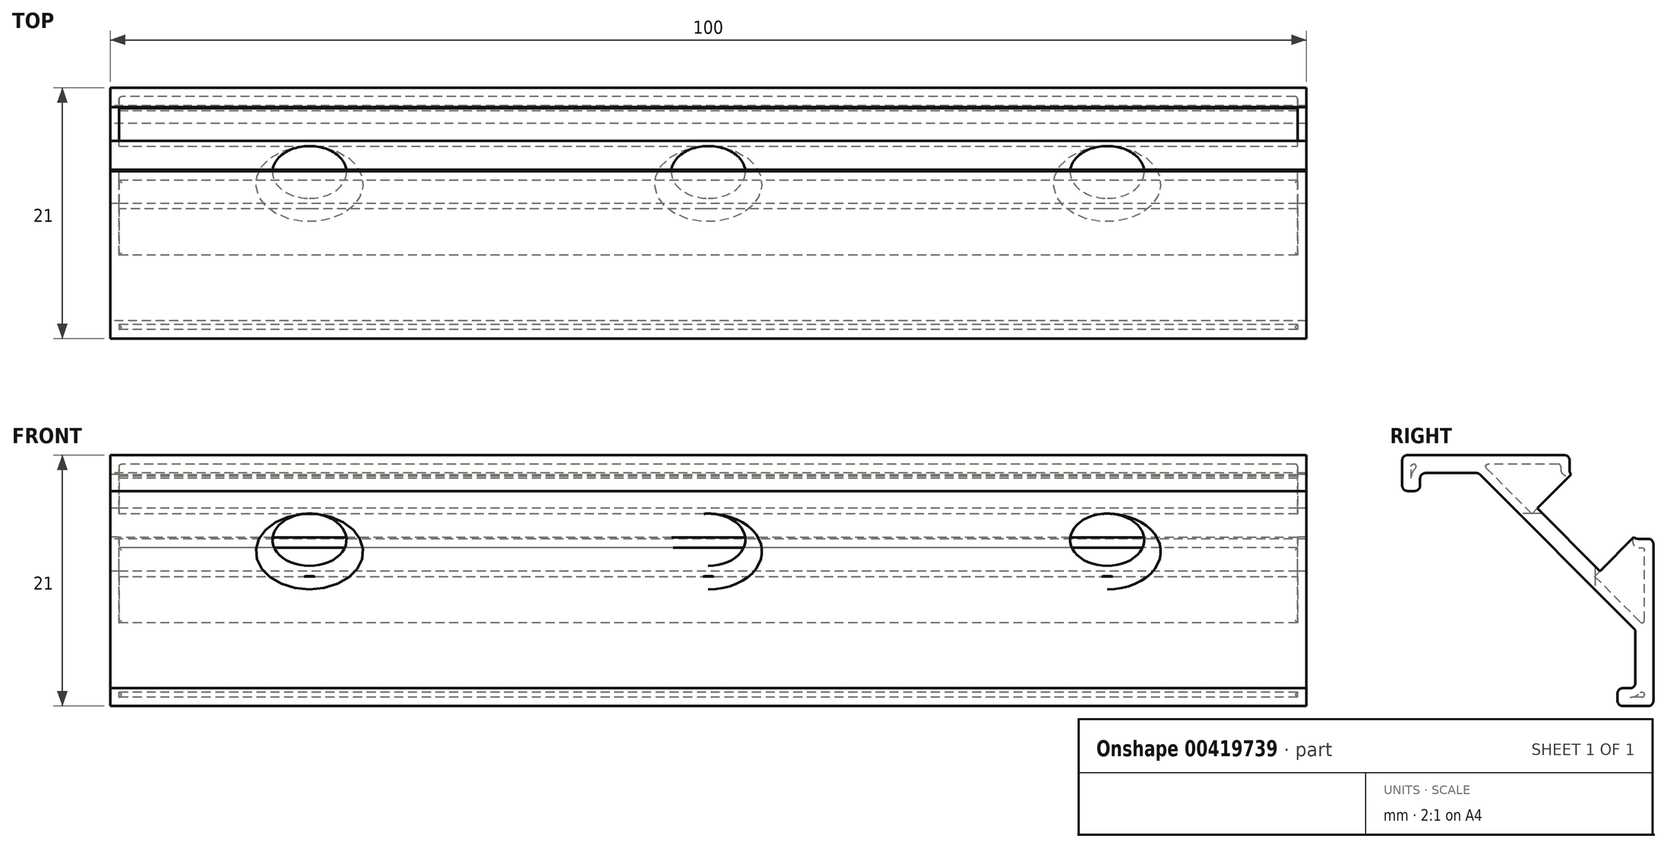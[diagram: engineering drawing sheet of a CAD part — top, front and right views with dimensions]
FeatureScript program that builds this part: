
annotation { "Feature Type Name" : "Feature", "Feature Type Description" : "" }
export const myFeature = defineFeature(function(context is Context, id is Id, definition is map)
    precondition{}
    {
        {
            var Q0;
            Q0=qCreatedBy(makeId("Right.planeOp"),FACE);
            var sketch = newSketch(context, id + "F0", { "sketchPlane" : qUnion([Q0])});
            skLineSegment(sketch, "E0.bottom", {"start": v(10.06, -10.5) * mm, "end": v(7.94, -10.5) * mm});
            skLineSegment(sketch, "E0.top", {"start": v(3.06, 10.5) * mm, "end": v(-10.06, 10.5) * mm});
            skLineSegment(sketch, "E0.left", {"start": v(10.5, -10.06) * mm, "end": v(10.5, 3.06) * mm});
            skPoint(sketch, "E0.middle", {"position": v(0, 0) * mm});
            skPoint(sketch, "E1.orphan", {"position": v(10.5, 10.5) * mm});
            skLineSegment(sketch, "E2.0", {"start": v(-4.3, 9) * mm, "end": v(-8.56, 9) * mm});
            skLineSegment(sketch, "E3.0", {"start": v(-4, 8.87) * mm, "end": v(8.87, -4) * mm});
            skLineSegment(sketch, "E4.0", {"start": v(9, -8.56) * mm, "end": v(9, -4.3) * mm});
            skLineSegment(sketch, "E5.0", {"start": v(8.56, -9) * mm, "end": v(7.94, -9) * mm});
            skLineSegment(sketch, "E6", {"start": v(3.5, 10.06) * mm, "end": v(3.5, 9.18) * mm});
            skLineSegment(sketch, "E7", {"start": v(9.18, 3.5) * mm, "end": v(10.06, 3.5) * mm});
            skLineSegment(sketch, "E8", {"start": v(-10.06, 7.5) * mm, "end": v(-9.44, 7.5) * mm});
            skLineSegment(sketch, "E9", {"start": v(7.5, -10.06) * mm, "end": v(7.5, -9.44) * mm});
            skLineSegment(sketch, "E10.trimOffspring", {"start": v(-9, 7.94) * mm, "end": v(-9, 8.56) * mm});
            skLineSegment(sketch, "E11.trimOffspring", {"start": v(-10.5, 7.94) * mm, "end": v(-10.5, 10.06) * mm});
            skPoint(sketch, "E12.trimOffspring.end.orphan", {"position": v(-10.5, -10.5) * mm});
            skLineSegment(sketch, "E13", {"start": v(3.63, 8.87) * mm, "end": v(8.87, 3.63) * mm});
            skPoint(sketch, "E14.visualSharp", {"position": v(3.5, 10.5) * mm});
            skArc(sketch, "E14.filletArc", {"start": v(3.5, 10.06) * mm, "mid": v(3.37, 10.37) * mm, "end": v(3.06, 10.5) * mm});
            skPoint(sketch, "E15.visualSharp", {"position": v(10.5, 3.5) * mm});
            skArc(sketch, "E15.filletArc", {"start": v(10.5, 3.06) * mm, "mid": v(10.37, 3.37) * mm, "end": v(10.06, 3.5) * mm});
            skPoint(sketch, "E16.visualSharp", {"position": v(3.5, 9) * mm});
            skArc(sketch, "E16.filletArc", {"start": v(3.5, 9.18) * mm, "mid": v(3.53, 9.01) * mm, "end": v(3.63, 8.87) * mm});
            skPoint(sketch, "E17.visualSharp", {"position": v(9, 3.5) * mm});
            skArc(sketch, "E17.filletArc", {"start": v(8.87, 3.63) * mm, "mid": v(9.01, 3.53) * mm, "end": v(9.18, 3.5) * mm});
            skPoint(sketch, "E18.orphan", {"position": v(-3.5, 10.5) * mm});
            skPoint(sketch, "E19.orphan", {"position": v(10.5, -3.5) * mm});
            skPoint(sketch, "E20.visualSharp", {"position": v(-4.12, 9) * mm});
            skArc(sketch, "E20.filletArc", {"start": v(-4, 8.87) * mm, "mid": v(-4.14, 8.97) * mm, "end": v(-4.3, 9) * mm});
            skPoint(sketch, "E21.visualSharp", {"position": v(-9, 9) * mm});
            skArc(sketch, "E21.filletArc", {"start": v(-8.56, 9) * mm, "mid": v(-8.87, 8.87) * mm, "end": v(-9, 8.56) * mm});
            skPoint(sketch, "E22.visualSharp", {"position": v(-9, 7.5) * mm});
            skArc(sketch, "E22.filletArc", {"start": v(-9.44, 7.5) * mm, "mid": v(-9.13, 7.63) * mm, "end": v(-9, 7.94) * mm});
            skPoint(sketch, "E23.visualSharp", {"position": v(-10.5, 7.5) * mm});
            skArc(sketch, "E23.filletArc", {"start": v(-10.5, 7.94) * mm, "mid": v(-10.37, 7.63) * mm, "end": v(-10.06, 7.5) * mm});
            skPoint(sketch, "E24.visualSharp", {"position": v(-10.5, 10.5) * mm});
            skArc(sketch, "E24.filletArc", {"start": v(-10.06, 10.5) * mm, "mid": v(-10.37, 10.37) * mm, "end": v(-10.5, 10.06) * mm});
            skPoint(sketch, "E25.visualSharp", {"position": v(9, -4.12) * mm});
            skArc(sketch, "E25.filletArc", {"start": v(9, -4.3) * mm, "mid": v(8.97, -4.14) * mm, "end": v(8.87, -4) * mm});
            skPoint(sketch, "E26.visualSharp", {"position": v(9, -9) * mm});
            skArc(sketch, "E26.filletArc", {"start": v(8.56, -9) * mm, "mid": v(8.87, -8.87) * mm, "end": v(9, -8.56) * mm});
            skPoint(sketch, "E27.visualSharp", {"position": v(7.5, -9) * mm});
            skArc(sketch, "E27.filletArc", {"start": v(7.94, -9) * mm, "mid": v(7.63, -9.13) * mm, "end": v(7.5, -9.44) * mm});
            skPoint(sketch, "E28.visualSharp", {"position": v(7.5, -10.5) * mm});
            skArc(sketch, "E28.filletArc", {"start": v(7.5, -10.06) * mm, "mid": v(7.63, -10.37) * mm, "end": v(7.94, -10.5) * mm});
            skPoint(sketch, "E29.visualSharp", {"position": v(10.5, -10.5) * mm});
            skArc(sketch, "E29.filletArc", {"start": v(10.06, -10.5) * mm, "mid": v(10.37, -10.37) * mm, "end": v(10.5, -10.06) * mm});
            skSolve(sketch);
        }
        {
            var Q0;
            Q0 = qSketchRegion(id + "F0", true);
            extrude(context, id + "F1", {"entities" : qUnion([Q0]), "depth" : 100 * mm});
        }
        {
            var Q0;
            Q0=makeQuery(id+"F1.opExtrude","SWEPT_FACE",FACE,{"disambiguationData":[OSD([sQuery(id+"F0.wireOp",EDGE,"E13")])]});
            extrude(context, id + "F2", {"entities" : qUnion([Q0]), "operationType" : NewBodyOperationType.REMOVE, "oppositeDirection" : true, "depth" : 4 * mm});
        }
        {
            var Q0;
            Q0=makeQuery(id+"F2.boolean.opBoolean","COPY",FACE,{"derivedFrom":makeQuery(id+"F2.opExtrude","SWEPT_FACE",FACE,{"disambiguationData":[OSD([sQuery(id+"F0.wireOp",EDGE,"E13"),sQuery(id+"F0.wireOp",EDGE,"E16.filletArc")])]})});
            var Q1;
            Q1=makeQuery(id+"F2.boolean.opBoolean","COPY",FACE,{"derivedFrom":makeQuery(id+"F2.opExtrude","SWEPT_FACE",FACE,{"disambiguationData":[OSD([sQuery(id+"F0.wireOp",EDGE,"E13"),sQuery(id+"F0.wireOp",EDGE,"E17.filletArc")])]})});
            shell(context, id + "F3", {"entities" : qUnion([Q0, Q1]), "thickness" : .75 * mm});
        }
        {
            var Q0;
            Q0=makeQuery(id+"F3.opShell","OFFSET_FACE",FACE,{"disambiguationData":[OSD([sQuery(id+"F0.wireOp",EDGE,"E0.top")])]});
            var Q1;
            Q1=makeQuery(id+"F3.opShell","OFFSET_FACE",FACE,{"disambiguationData":[OSD([sQuery(id+"F0.wireOp",EDGE,"E0.left")])]});
            fillet(context, id + "F4", {"entities" : qUnion([Q0, Q1]), "radius" : 0.2 * mm, "tangentPropagation" : true, "allowEdgeOverflow" : false});
        }
        {
            var Q0;
            {var subQ0=sQuery(id+"F0.wireOp",EDGE,"E17.filletArc");var subQ1=sQuery(id+"F0.wireOp",EDGE,"E13");Q0=makeQuery(id+"F3.opShell","OFFSET_EDGE",EDGE,{"disambiguationData":[OSD([subQ1,subQ0]),TDD([makeQuery(id+"F2.boolean.opBoolean","MERGE",EDGE,{"derivedFrom":[makeQuery(id+"F1.opExtrude","SWEPT_EDGE",EDGE,{"disambiguationData":[OSD([subQ1,subQ0])]}),makeQuery(id+"F2.opExtrude","CAP_EDGE",EDGE,{"disambiguationData":[OSD([subQ1,subQ0])],"isStart":true})]})])]});}
            var Q1;
            {var subQ0=sQuery(id+"F0.wireOp",EDGE,"E16.filletArc");var subQ1=sQuery(id+"F0.wireOp",EDGE,"E13");Q1=makeQuery(id+"F3.opShell","OFFSET_EDGE",EDGE,{"disambiguationData":[OSD([subQ1,subQ0]),TDD([makeQuery(id+"F2.boolean.opBoolean","MERGE",EDGE,{"derivedFrom":[makeQuery(id+"F1.opExtrude","SWEPT_EDGE",EDGE,{"disambiguationData":[OSD([subQ1,subQ0])]}),makeQuery(id+"F2.opExtrude","CAP_EDGE",EDGE,{"disambiguationData":[OSD([subQ1,subQ0])],"isStart":true})]})])]});}
            fillet(context, id + "F5", {"entities" : qUnion([Q0, Q1]), "radius" : .55 * mm, "tangentPropagation" : true, "allowEdgeOverflow" : false});
        }
        {
            var Q0;
            Q0=makeQuery(id+"F1.opExtrude","SWEPT_FACE",FACE,{"disambiguationData":[OSD([sQuery(id+"F0.wireOp",EDGE,"E3.0")])]});
            var sketch = newSketch(context, id + "F6", { "sketchPlane" : qUnion([Q0])});
            skLineSegment(sketch, "E30.0", {"start": v(50, 9.1) * mm, "end": v(50, -9.1) * mm, "construction": true});
            skLineSegment(sketch, "E31.0", {"start": v(100, 0) * mm, "end": v(0, 0) * mm, "construction": true});
            skLineSegment(sketch, "E32.0", {"start": v(83.34, 9.1) * mm, "end": v(83.34, -9.1) * mm, "construction": true});
            skLineSegment(sketch, "E33.MirrorCS", {"start": v(16.66, 9.1) * mm, "end": v(16.66, -9.1) * mm, "construction": true});
            skPoint(sketch, "E34", {"position": v(83.34, 0) * mm});
            skPoint(sketch, "E35", {"position": v(50, 0) * mm});
            skPoint(sketch, "E36", {"position": v(16.66, 0) * mm});
            skSolve(sketch);
        }
        {
            var Q0;
            Q0=sQuery(id+"F6.wireOp",VERTEX,"E35");
            var Q1;
            Q1=sQuery(id+"F6.wireOp",VERTEX,"E34");
            var Q2;
            Q2=sQuery(id+"F6.wireOp",VERTEX,"E36");
            var Q3;
            Q3=makeQuery(id+"F1.opExtrude","SWEPT_BODY",BODY,{"disambiguationData":[OSD([sQuery(id+"F0.wireOp",EDGE,"E0.bottom"),sQuery(id+"F0.wireOp",EDGE,"E0.top"),sQuery(id+"F0.wireOp",EDGE,"E0.left"),sQuery(id+"F0.wireOp",EDGE,"E2.0"),sQuery(id+"F0.wireOp",EDGE,"E3.0"),sQuery(id+"F0.wireOp",EDGE,"E4.0"),sQuery(id+"F0.wireOp",EDGE,"E5.0"),sQuery(id+"F0.wireOp",EDGE,"E6"),sQuery(id+"F0.wireOp",EDGE,"E7"),sQuery(id+"F0.wireOp",EDGE,"E8"),sQuery(id+"F0.wireOp",EDGE,"E9"),sQuery(id+"F0.wireOp",EDGE,"E10.trimOffspring"),sQuery(id+"F0.wireOp",EDGE,"E11.trimOffspring"),sQuery(id+"F0.wireOp",EDGE,"E13"),sQuery(id+"F0.wireOp",EDGE,"E14.filletArc"),sQuery(id+"F0.wireOp",EDGE,"E15.filletArc"),sQuery(id+"F0.wireOp",EDGE,"E16.filletArc"),sQuery(id+"F0.wireOp",EDGE,"E17.filletArc"),sQuery(id+"F0.wireOp",EDGE,"E20.filletArc"),sQuery(id+"F0.wireOp",EDGE,"E21.filletArc"),sQuery(id+"F0.wireOp",EDGE,"E22.filletArc"),sQuery(id+"F0.wireOp",EDGE,"E23.filletArc"),sQuery(id+"F0.wireOp",EDGE,"E24.filletArc"),sQuery(id+"F0.wireOp",EDGE,"E25.filletArc"),sQuery(id+"F0.wireOp",EDGE,"E26.filletArc"),sQuery(id+"F0.wireOp",EDGE,"E27.filletArc"),sQuery(id+"F0.wireOp",EDGE,"E28.filletArc"),sQuery(id+"F0.wireOp",EDGE,"E29.filletArc")])]});
            hole(context, id + "F7", {"style" : HoleStyle.C_SINK, "endStyle" : HoleEndStyle.THROUGH, "standardTappedOrClearance" : lookupTablePath({ "standard" : "ISO", "fit" : "Normal", "size" : "M4", "type" : "Clearance" }), "standardBlindInLast" : lookupTablePath({ "fit" : "Standard", "standard" : "ISO", "size" : "M4", "type" : "Clearance" }), "holeDiameter" : 4.4 * mm, "cSinkDiameter" : 8.96 * mm, "cSinkAngle" : 90 * degree, "isTappedThrough" : true, "tappedDepth" : 12 * mm, "tapClearance" : 3, "locations" : qUnion([Q0, Q1, Q2]), "scope" : qUnion([Q3])});
        }
    });
